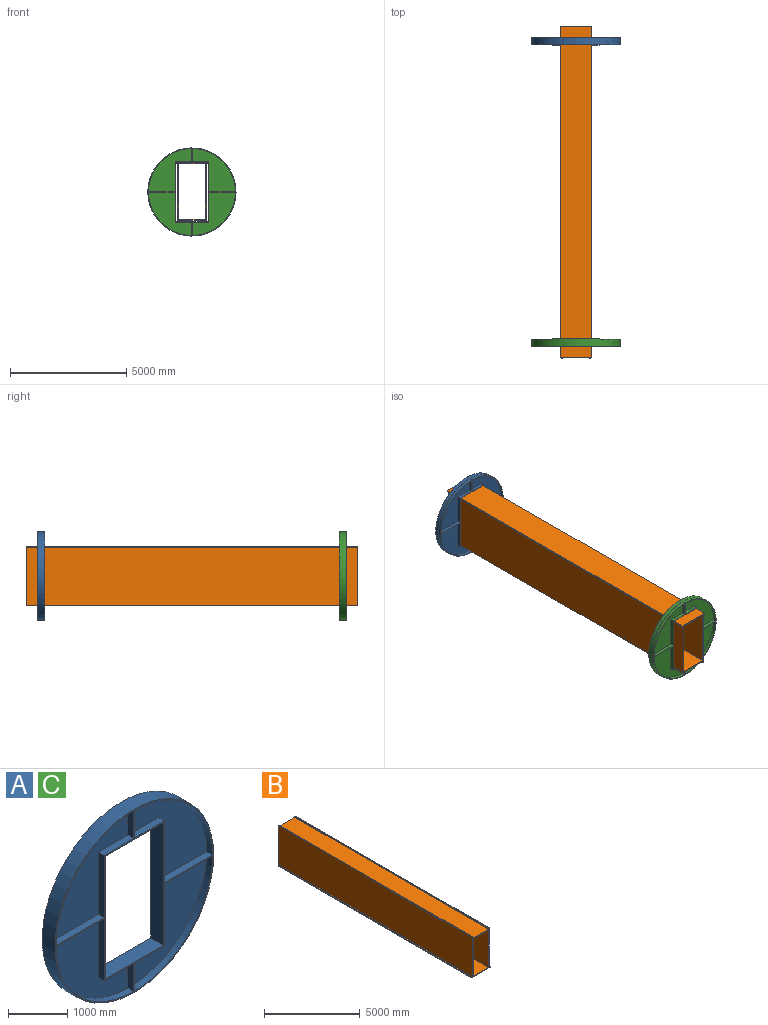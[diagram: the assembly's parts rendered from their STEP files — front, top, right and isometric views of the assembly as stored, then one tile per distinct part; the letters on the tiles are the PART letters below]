
ASSEMBLY  parts=3 mates=2
PART A: 59 faces, bbox 3794.3x304.8x3794.3 mm
  f0: plane 1871.68x1859.03mm, normal (0,1,0), area 1802159.4mm2, adj f1,f9,f11,f48,f57
  f1: plane 1284.17x139.7mm, normal (1,0,0), area 179399mm2, adj f0,f11,f23,f57
  f2: cylinder r=1871.73mm len=1871.68mm, axis (0,1,0), area 407192.8mm2, adj f8,f23,f52,f53,f58
  f3: plane 1858.98x1858.98mm, normal (0,1,0), area 1794859.1mm2, adj f6,f10,f36,f51,f56
  f4: plane 1284.17x139.7mm, normal (-1,0,0), area 179399mm2, adj f7,f23,f35,f55
  f5: cylinder r=1871.73mm len=1884.26mm, axis (0,1,0), area 407177mm2, adj f7,f23,f47,f50,f55
  f6: plane 733.35x139.7mm, normal (0,0,-1), area 98911.6mm2, adj f3,f23,f36,f51,f54
  f7: plane 1858.98x1858.98mm, normal (0,1,0), area 1794859.1mm2, adj f4,f5,f35,f47,f55
  f8: plane 1871.68x1859.03mm, normal (0,1,0), area 1802159.4mm2, adj f2,f37,f38,f52,f58
  f9: cylinder r=1871.73mm len=1871.68mm, axis (0,1,0), area 407192.8mm2, adj f0,f23,f48,f49,f57
  f10: cylinder r=1871.73mm len=1884.26mm, axis (0,1,0), area 407177mm2, adj f3,f23,f51,f54,f56
  f11: plane 720.78x139.7mm, normal (0,0,1), area 98927.4mm2, adj f0,f1,f23,f48,f49
  f12: plane 1858.98x1858.98mm, normal (0,-1,0), area 1794859mm2, adj f13,f20,f33,f41,f46
  f13: plane 708.08x139.7mm, normal (0,0,-1), area 98918.2mm2, adj f12,f29,f33,f46
  f14: cylinder r=1871.73mm len=1858.98mm, axis (0,-1,0), area 407183.6mm2, adj f22,f29,f39,f45
  f15: plane 1858.98x1858.98mm, normal (0,-1,0), area 1794859mm2, adj f21,f30,f34,f40,f43
  f16: plane 708.08x139.7mm, normal (0,0,1), area 98918.2mm2, adj f18,f19,f29,f44
  f17: cylinder r=1871.73mm len=1858.98mm, axis (0,-1,0), area 407183.6mm2, adj f18,f29,f42,f44
  f18: plane 1858.98x1858.98mm, normal (0,-1,0), area 1794859mm2, adj f16,f17,f19,f42,f44
  f19: plane 1284.17x139.7mm, normal (-1,0,0), area 179399mm2, adj f16,f18,f29,f42
  f20: cylinder r=1871.73mm len=1858.98mm, axis (0,-1,0), area 407183.6mm2, adj f12,f29,f41,f46
  f21: plane 1284.17x139.7mm, normal (1,0,0), area 179399mm2, adj f15,f29,f30,f40
  f22: plane 1858.98x1858.98mm, normal (0,-1,0), area 1794859mm2, adj f14,f31,f32,f39,f45
  f23: plane 3794.25x3794.25mm, normal (0,1,0), area 561621.1mm2, adj f1,f2,f4,f5,f6,f9,f10,f11
  f24: plane 1390.75x304.8mm, normal (0,0,-1), area 423901.1mm2, adj f23,f25,f27,f29
  f25: plane 2542.95x304.8mm, normal (-1,0,0), area 775090.1mm2, adj f23,f24,f26,f29
  f26: plane 1390.75x304.8mm, normal (0,0,1), area 423901.1mm2, adj f23,f25,f27,f29
  f27: plane 2542.95x304.8mm, normal (1,0,0), area 775090.1mm2, adj f23,f24,f26,f29
  f28: cylinder r=1897.13mm len=3794.25mm, axis (0,1,0), area 3633214.2mm2, adj f23,f29
  f29: plane 3794.25x3794.25mm, normal (0,-1,0), area 590822.9mm2, adj f13,f14,f16,f17,f19,f20,f21,f24
  f30: plane 708.08x139.7mm, normal (0,0,1), area 98918.2mm2, adj f15,f21,f29,f43
  f31: plane 1284.17x139.7mm, normal (1,0,0), area 179399mm2, adj f22,f29,f32,f39
  f32: plane 708.08x139.7mm, normal (0,0,-1), area 98918.2mm2, adj f22,f29,f31,f45
  f33: plane 1284.17x139.7mm, normal (-1,0,0), area 179399mm2, adj f12,f13,f29,f41
  f34: cylinder r=1871.73mm len=1858.98mm, axis (0,-1,0), area 407183.6mm2, adj f15,f29,f40,f43
  f35: plane 733.35x139.7mm, normal (0,0,1), area 98911.6mm2, adj f4,f7,f23,f47,f50
  f36: plane 1284.17x139.7mm, normal (-1,0,0), area 179399mm2, adj f3,f6,f23,f56
  f37: plane 720.78x139.7mm, normal (0,0,-1), area 98927.4mm2, adj f8,f23,f38,f52,f53
  f38: plane 1284.17x139.7mm, normal (1,0,0), area 179399mm2, adj f8,f23,f37,f58
  f39: plane 1150.91x139.7mm, normal (0,0,-1), area 160781.7mm2, adj f14,f22,f29,f31
  f40: plane 1150.91x139.7mm, normal (0,0,1), area 160781.7mm2, adj f15,f21,f29,f34
  f41: plane 1150.91x139.7mm, normal (0,0,-1), area 160781.7mm2, adj f12,f20,f29,f33
  f42: plane 1150.91x139.7mm, normal (0,0,1), area 160781.7mm2, adj f17,f18,f19,f29
  f43: plane 574.81x139.7mm, normal (1,0,0), area 80300.9mm2, adj f15,f29,f30,f34
  f44: plane 574.81x139.7mm, normal (-1,0,0), area 80300.9mm2, adj f16,f17,f18,f29
  f45: plane 574.81x139.7mm, normal (1,0,0), area 80300.9mm2, adj f14,f22,f29,f32
  f46: plane 574.81x139.7mm, normal (-1,0,0), area 80300.9mm2, adj f12,f13,f20,f29
  f47: plane 574.81x139.54mm, normal (-1,0,0), area 80209.6mm2, adj f5,f7,f35,f50
  f48: plane 574.85x12.7mm, normal (0.01,-1,0), area 7300.4mm2, adj f0,f9,f11,f49
  f49: plane 574.81x139.62mm, normal (1,0,0), area 80255.4mm2, adj f9,f11,f48,f50
  f50: plane 574.85x25.4mm, normal (-0.01,1,0), area 14600.9mm2, adj f5,f35,f47,f49
  f51: plane 574.81x139.54mm, normal (-1,0,0), area 80209.6mm2, adj f3,f6,f10,f54
  f52: plane 574.85x12.7mm, normal (0.01,-1,0), area 7300.4mm2, adj f2,f8,f37,f53
  f53: plane 574.81x139.62mm, normal (1,0,0), area 80255.4mm2, adj f2,f37,f52,f54
  f54: plane 574.85x25.4mm, normal (-0.01,1,0), area 14600.9mm2, adj f6,f10,f51,f53
  f55: plane 1150.91x139.7mm, normal (0,0,1), area 160781.7mm2, adj f4,f5,f7,f23
  f56: plane 1150.91x139.7mm, normal (0,0,-1), area 160781.7mm2, adj f3,f10,f23,f36
  f57: plane 1150.91x139.7mm, normal (0,0,1), area 160781.7mm2, adj f0,f1,f9,f23
  f58: plane 1150.91x139.7mm, normal (0,0,-1), area 160781.7mm2, adj f2,f8,f23,f38
PART B: 18 faces, bbox 1346.2x14285.9x2552.7 mm
  f0: plane 14285.91x63.5mm, normal (0,0,1), area 907155.4mm2, adj f1,f15,f16,f17
  f1: plane 14285.91x2501.9mm, normal (1,0,0), area 35741924.5mm2, adj f0,f2,f16,f17
  f2: plane 14285.91x38.1mm, normal (0,0,1), area 544293.3mm2, adj f1,f3,f16,f17
  f3: plane 14285.91x63.5mm, normal (-1,0,0), area 907155.4mm2, adj f2,f4,f16,f17
  f4: plane 14285.91x1143mm, normal (0,0,1), area 16328798mm2, adj f3,f5,f16,f17
  f5: plane 14285.91x63.5mm, normal (1,0,0), area 907155.4mm2, adj f4,f6,f16,f17
  f6: plane 14285.91x38.1mm, normal (0,0,1), area 544293.3mm2, adj f5,f7,f16,f17
  f7: plane 14285.91x2501.9mm, normal (-1,0,0), area 35741924.5mm2, adj f6,f8,f16,f17
  f8: plane 14285.91x63.5mm, normal (0,0,1), area 907155.4mm2, adj f7,f9,f16,f17
  f9: plane 14285.91x50.8mm, normal (-1,0,0), area 725724.4mm2, adj f8,f10,f16,f17
  f10: plane 14285.91x1346.2mm, normal (0,0,-1), area 19231695.4mm2, adj f9,f15,f16,f17
  f11: plane 14285.91x2387.6mm, normal (-1,0,0), area 34109044.7mm2, adj f12,f14,f16,f17
  f12: plane 14285.91x1143mm, normal (0,0,1), area 16328798mm2, adj f11,f13,f16,f17
  f13: plane 14285.91x2387.6mm, normal (1,0,0), area 34109044.7mm2, adj f12,f14,f16,f17
  f14: plane 14285.91x1143mm, normal (0,0,-1), area 16328798mm2, adj f11,f13,f16,f17
  f15: plane 14285.91x50.8mm, normal (1,0,0), area 725724.4mm2, adj f0,f10,f16,f17
  f16: plane 2552.7x1346.2mm, normal (0,-1,0), area 317096.1mm2, adj f0,f1,f2,f3,f4,f5,f6,f7
  f17: plane 2552.7x1346.2mm, normal (0,1,0), area 317096.1mm2, adj f0,f1,f2,f3,f4,f5,f6,f7
PART C: same geometry as A
PLACE A t=(-2659.17,-1051.91,496.45)mm
PLACE B rot(axis=(0,1,0),180deg) t=(-2622.26,-543.91,496.33)mm
PLACE C rot(axis=(1,0,0),180deg) t=(-2659.17,-14321.82,496.45)mm
MATE fastened B.f10 <-> A.f24  axis (0,0,1) through (-2659.17,-543.91,1767.92)mm
MATE fastened C.f26 <-> B.f10  axis (0,0,-1) through (-2659.17,-14321.82,1767.92)mm
